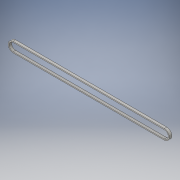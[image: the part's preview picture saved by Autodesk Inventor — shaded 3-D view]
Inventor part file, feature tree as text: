
AUTODESK INVENTOR PART (.ipt)
format: ipt  version: 2016 (Build 200138000, 138)  size: 109,568 bytes
history: native  units: in
note: dims shown in document units (in); Inventor stores cm internally (conversion verified against a paired STEP export)
features: fillet x4, extrude x1, shell x1, sketch x1
ambient origin geometry x8: Origin, YZ Plane, XZ Plane, XY Plane, X Axis, Y Axis, Z Axis, Center Point
bodies: Solid1 (feature_tree)
feature tree (7):
  extrude  "Extrusion1"  Depth=1.0in
  fillet  "Fillet1"  Radius=0.25in
  fillet  "Fillet2"  Radius=0.5in
  fillet  "Fillet3"  Radius=0.5in
  fillet  "Fillet4"  Radius=0.5in
  shell  "Shell1"  Thickness=0.5in
  sketch  "Sketch1"  dims[d0=16.0in d1=1.0in d2=0.25in d3=0.0in d4=0.5in d5=0.5in d6=0.5in d7=0.5in d8=0.1in]
